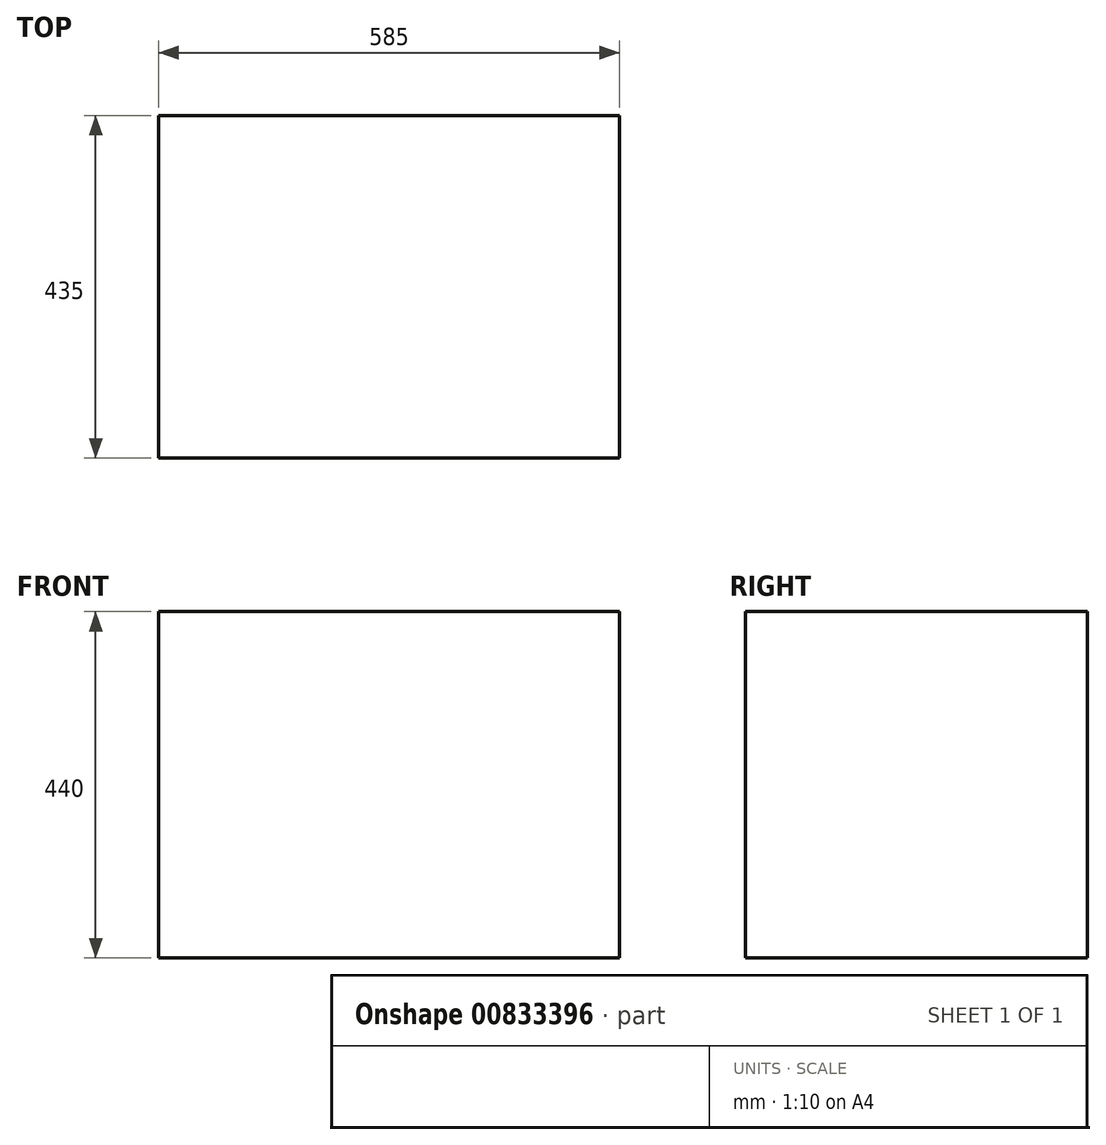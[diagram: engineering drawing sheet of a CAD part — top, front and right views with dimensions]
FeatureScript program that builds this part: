
annotation { "Feature Type Name" : "Feature", "Feature Type Description" : "" }
export const myFeature = defineFeature(function(context is Context, id is Id, definition is map)
    precondition{}
    {
        {
            var Q0;
            Q0=qCreatedBy(makeId("Top.planeOp"),FACE);
            var sketch = newSketch(context, id + "F0", { "sketchPlane" : qUnion([Q0])});
            skLineSegment(sketch, "E0.bottom", {"start": v(292.5, -217.5) * mm, "end": v(-292.5, -217.5) * mm});
            skLineSegment(sketch, "E0.top", {"start": v(292.5, 217.5) * mm, "end": v(-292.5, 217.5) * mm});
            skLineSegment(sketch, "E0.left", {"start": v(292.5, -217.5) * mm, "end": v(292.5, 217.5) * mm});
            skLineSegment(sketch, "E0.right", {"start": v(-292.5, -217.5) * mm, "end": v(-292.5, 217.5) * mm});
            skPoint(sketch, "E0.middle", {"position": v(0, 0) * mm});
            skSolve(sketch);
        }
        {
            var Q0;
            Q0=makeQuery(id+"F0.imprint","IMPRINT",FACE,{"disambiguationData":[TD([[makeQuery(id+"F0.imprint","IMPRINT",EDGE,{"derivedFrom":sQuery(id+"F0.wireOp",EDGE,"E0.bottom")}),-1.0]])]});
            extrude(context, id + "F1", {"entities" : qUnion([Q0]), "depth" : 440 * mm, "offsetDistance" : 25 * mm});
        }
    });
